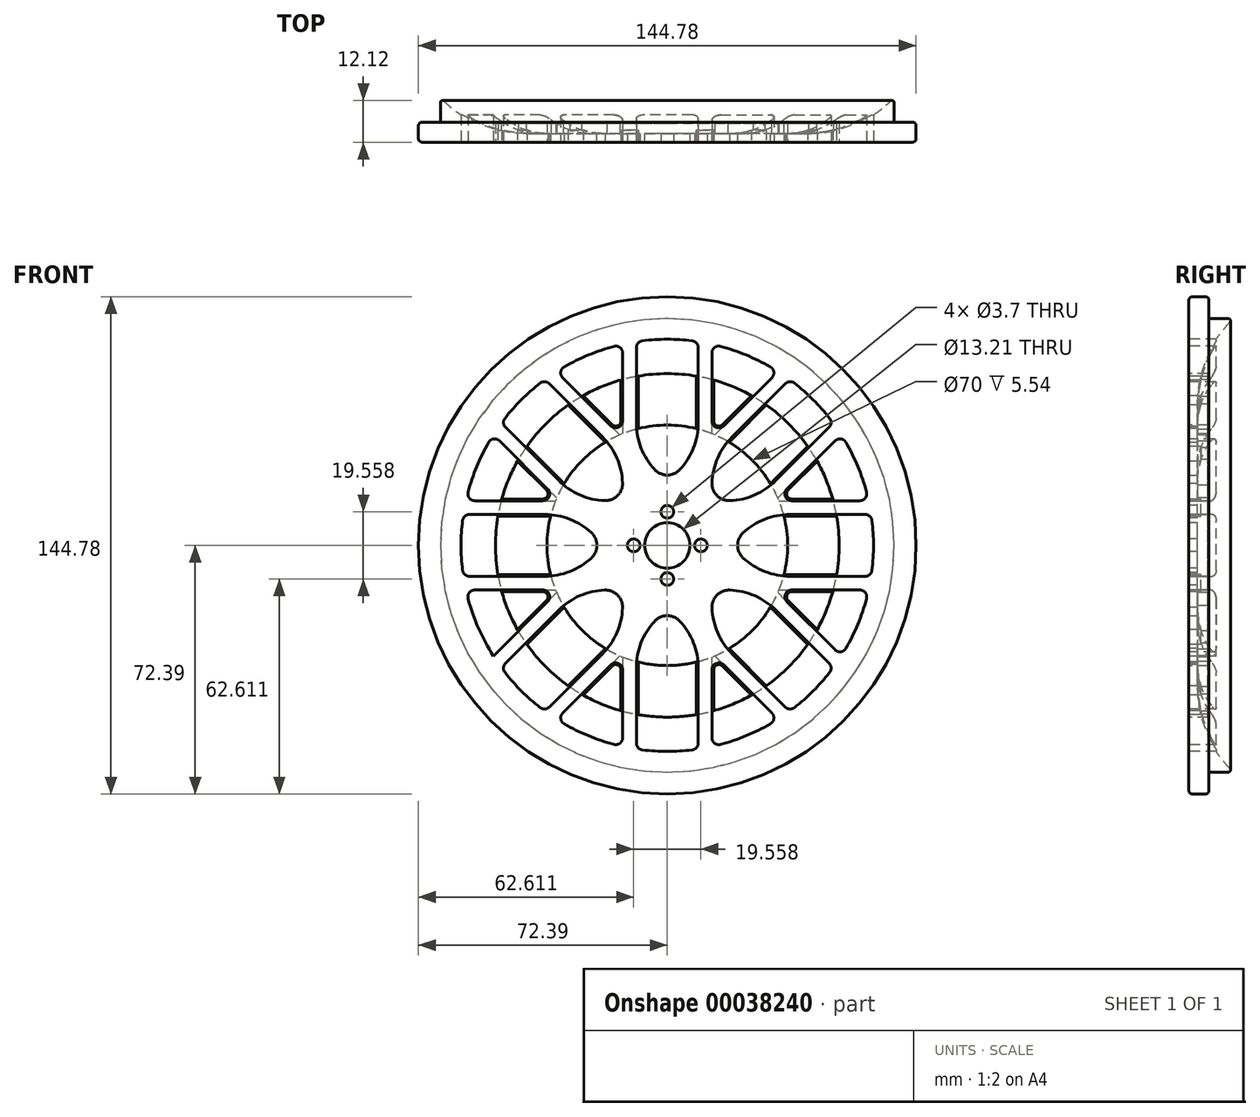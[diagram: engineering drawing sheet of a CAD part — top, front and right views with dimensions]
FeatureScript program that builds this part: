
annotation { "Feature Type Name" : "Feature", "Feature Type Description" : "" }
export const myFeature = defineFeature(function(context is Context, id is Id, definition is map)
    precondition{}
    {
        {
            var Q0;
            Q0=qCreatedBy(makeId("Right.planeOp"),FACE);
            var sketch = newSketch(context, id + "F0", { "sketchPlane" : qUnion([Q0])});
            skLineSegment(sketch, "E0", {"start": v(0, 6.6) * mm, "end": v(2.54, 6.6) * mm});
            skLineSegment(sketch, "E1", {"start": v(2.54, 6.6) * mm, "end": v(2.54, 42) * mm});
            skLineSegment(sketch, "E2", {"start": v(0, 6.6) * mm, "end": v(0, 66) * mm});
            skLineSegment(sketch, "E3", {"start": v(0, 66) * mm, "end": v(13, 66) * mm});
            skArc(sketch, "E4", {"start": v(2.54, 42) * mm, "mid": v(5.27, 55.1) * mm, "end": v(13, 66) * mm});
            skLineSegment(sketch, "E5", {"start": v(0, 0) * mm, "end": v(13, 0) * mm, "construction": true});
            skSolve(sketch);
        }
        {
            var Q0;
            Q0=makeQuery(id+"F0.imprint","IMPRINT",FACE,{"disambiguationData":[TD([[makeQuery(id+"F0.imprint","IMPRINT",EDGE,{"derivedFrom":sQuery(id+"F0.wireOp",EDGE,"E0")}),1.0]])]});
            var Q1;
            Q1=sQuery(id+"F0.wireOp",EDGE,"E5");
            revolve(context, id + "F1", {"entities" : qUnion([Q0]), "axis" : qUnion([Q1]), "revolveType" : RevolveType.FULL});
        }
        {
            var Q0;
            Q0=qCreatedBy(makeId("Front.planeOp"),FACE);
            var sketch = newSketch(context, id + "F2", { "sketchPlane" : qUnion([Q0])});
            skCircle(sketch, "E6", {"center": v(0, 0) * mm, "radius": 9.78 * mm, "construction": true});
            skPoint(sketch, "E7", {"position": v(0, 9.78) * mm});
            skPoint(sketch, "E8", {"position": v(0, -9.78) * mm});
            skPoint(sketch, "E9", {"position": v(9.78, 0) * mm});
            skPoint(sketch, "E10", {"position": v(-9.78, 0) * mm});
            skSolve(sketch);
        }
        {
            var Q0;
            Q0=sQuery(id+"F2.wireOp",VERTEX,"E7");
            var Q1;
            Q1=sQuery(id+"F2.wireOp",VERTEX,"E9");
            var Q2;
            Q2=sQuery(id+"F2.wireOp",VERTEX,"E8");
            var Q3;
            Q3=sQuery(id+"F2.wireOp",VERTEX,"E10");
            var Q4;
            Q4=makeQuery(id+"F1.opRevolve","SWEPT_BODY",BODY,{"disambiguationData":[OSD([sQuery(id+"F0.wireOp",EDGE,"E0"),sQuery(id+"F0.wireOp",EDGE,"E1"),sQuery(id+"F0.wireOp",EDGE,"E2"),sQuery(id+"F0.wireOp",EDGE,"E3"),sQuery(id+"F0.wireOp",EDGE,"E4")])]});
            hole(context, id + "F3", {"style" : HoleStyle.SIMPLE, "holeDiameter" : 3.7 * mm, "endStyle" : HoleEndStyle.THROUGH, "locations" : qUnion([Q0, Q1, Q2, Q3]), "scope" : qUnion([Q4])});
        }
        {
            var Q0;
            Q0=makeQuery(id+"F1.opRevolve","SWEPT_FACE",FACE,{"disambiguationData":[OSD([sQuery(id+"F0.wireOp",EDGE,"E2")])]});
            var sketch = newSketch(context, id + "F4", { "sketchPlane" : qUnion([Q0])});
            skArc(sketch, "E11", {"start": v(-35.58, 48.31) * mm, "mid": v(-42.43, 42.43) * mm, "end": v(-48.31, 35.58) * mm});
            skLineSegment(sketch, "E12", {"start": v(-58.57, 13) * mm, "end": v(-31.38, 13) * mm});
            skLineSegment(sketch, "E13", {"start": v(-58.57, -13) * mm, "end": v(-31.38, -13) * mm});
            skLineSegment(sketch, "E14", {"start": v(-13, 58.57) * mm, "end": v(-13, 31.38) * mm});
            skLineSegment(sketch, "E15", {"start": v(13, -58.57) * mm, "end": v(13, -31.38) * mm});
            skLineSegment(sketch, "E16", {"start": v(-50.61, 32.23) * mm, "end": v(-31.38, 13) * mm});
            skLineSegment(sketch, "E17", {"start": v(-32.23, 50.61) * mm, "end": v(-13, 31.38) * mm});
            skLineSegment(sketch, "E18", {"start": v(-50.61, -32.23) * mm, "end": v(-31.38, -13) * mm});
            skLineSegment(sketch, "E19", {"start": v(-32.23, -50.61) * mm, "end": v(-13, -31.38) * mm});
            skLineSegment(sketch, "E20.trimOffspring", {"start": v(0, 18.38) * mm, "end": v(9, 27.38) * mm});
            skLineSegment(sketch, "E21.trimOffspring", {"start": v(13, 13) * mm, "end": v(25.73, 13) * mm});
            skLineSegment(sketch, "E22.trimOffspring", {"start": v(18.38, 0) * mm, "end": v(27.38, -9) * mm});
            skLineSegment(sketch, "E23.trimOffspring", {"start": v(13, 13) * mm, "end": v(13, 25.73) * mm});
            skLineSegment(sketch, "E24.trimOffspring", {"start": v(18.38, 0) * mm, "end": v(27.38, 9) * mm});
            skLineSegment(sketch, "E25.trimOffspring", {"start": v(13, -13) * mm, "end": v(25.73, -13) * mm});
            skLineSegment(sketch, "E26.trimOffspring", {"start": v(0, -18.38) * mm, "end": v(9, -27.38) * mm});
            skLineSegment(sketch, "E27.trimOffspring", {"start": v(-13, -13) * mm, "end": v(-13, -25.73) * mm});
            skLineSegment(sketch, "E28.0", {"start": v(-35.58, 48.31) * mm, "end": v(-13, 25.73) * mm});
            skCircle(sketch, "E29.0", {"center": v(0, 0) * mm, "radius": 71 * mm});
            skLineSegment(sketch, "E30.0", {"start": v(-48.31, 35.58) * mm, "end": v(-25.73, 13) * mm});
            skLineSegment(sketch, "E31.0", {"start": v(-9, 59.32) * mm, "end": v(-9, 27.38) * mm});
            skLineSegment(sketch, "E32.0", {"start": v(9, 27.38) * mm, "end": v(9, 59.32) * mm});
            skLineSegment(sketch, "E33.0", {"start": v(13, 25.73) * mm, "end": v(35.58, 48.31) * mm});
            skLineSegment(sketch, "E34.0", {"start": v(25.73, 13) * mm, "end": v(48.31, 35.58) * mm});
            skLineSegment(sketch, "E35.0", {"start": v(27.38, 9) * mm, "end": v(59.32, 9) * mm});
            skLineSegment(sketch, "E36.0", {"start": v(27.38, -9) * mm, "end": v(59.32, -9) * mm});
            skLineSegment(sketch, "E37.0", {"start": v(25.73, -13) * mm, "end": v(48.31, -35.58) * mm});
            skLineSegment(sketch, "E38.0", {"start": v(13, -25.73) * mm, "end": v(35.58, -48.31) * mm});
            skLineSegment(sketch, "E39.0", {"start": v(9, -59.32) * mm, "end": v(9, -27.38) * mm});
            skLineSegment(sketch, "E40.0", {"start": v(-9, -27.38) * mm, "end": v(-9, -59.32) * mm});
            skLineSegment(sketch, "E41.0", {"start": v(-35.58, -48.31) * mm, "end": v(-13, -25.73) * mm});
            skLineSegment(sketch, "E42.0", {"start": v(-48.31, -35.58) * mm, "end": v(-25.73, -13) * mm});
            skLineSegment(sketch, "E43.0", {"start": v(-59.32, -9) * mm, "end": v(-27.38, -9) * mm});
            skLineSegment(sketch, "E44.0", {"start": v(-59.32, 9) * mm, "end": v(-27.38, 9) * mm});
            skLineSegment(sketch, "E45.trimOffspring", {"start": v(-25.73, 13) * mm, "end": v(-13, 13) * mm});
            skLineSegment(sketch, "E46.trimOffspring", {"start": v(-27.38, 9) * mm, "end": v(-18.38, 0) * mm});
            skLineSegment(sketch, "E47.trimOffspring", {"start": v(-27.38, -9) * mm, "end": v(-18.38, 0) * mm});
            skLineSegment(sketch, "E48.trimOffspring", {"start": v(-25.73, -13) * mm, "end": v(-13, -13) * mm});
            skLineSegment(sketch, "E49.trimOffspring", {"start": v(-9, -27.38) * mm, "end": v(0, -18.38) * mm});
            skLineSegment(sketch, "E50.trimOffspring", {"start": v(-13, -31.38) * mm, "end": v(-13, -58.57) * mm});
            skLineSegment(sketch, "E51.trimOffspring", {"start": v(13, -31.38) * mm, "end": v(32.23, -50.61) * mm});
            skLineSegment(sketch, "E52.trimOffspring", {"start": v(13, -25.73) * mm, "end": v(13, -13) * mm});
            skLineSegment(sketch, "E53.trimOffspring", {"start": v(31.38, -13) * mm, "end": v(50.61, -32.23) * mm});
            skLineSegment(sketch, "E54.trimOffspring", {"start": v(31.38, -13) * mm, "end": v(58.57, -13) * mm});
            skLineSegment(sketch, "E55.trimOffspring", {"start": v(31.38, 13) * mm, "end": v(50.61, 32.23) * mm});
            skLineSegment(sketch, "E56.trimOffspring", {"start": v(31.38, 13) * mm, "end": v(58.57, 13) * mm});
            skLineSegment(sketch, "E57.trimOffspring", {"start": v(13, 31.38) * mm, "end": v(13, 58.57) * mm});
            skLineSegment(sketch, "E58.trimOffspring", {"start": v(13, 31.38) * mm, "end": v(32.23, 50.61) * mm});
            skLineSegment(sketch, "E59.trimOffspring", {"start": v(-9, 27.38) * mm, "end": v(0, 18.38) * mm});
            skLineSegment(sketch, "E60.trimOffspring", {"start": v(-13, 25.73) * mm, "end": v(-13, 13) * mm});
            skArc(sketch, "E61.trimOffspring", {"start": v(-50.61, 32.23) * mm, "mid": v(-55.43, 22.96) * mm, "end": v(-58.57, 13) * mm});
            skArc(sketch, "E62.trimOffspring", {"start": v(-13, 58.57) * mm, "mid": v(-22.96, 55.43) * mm, "end": v(-32.23, 50.61) * mm});
            skArc(sketch, "E63.trimOffspring", {"start": v(9, 59.32) * mm, "mid": v(0, 60) * mm, "end": v(-9, 59.32) * mm});
            skArc(sketch, "E64.trimOffspring", {"start": v(32.23, 50.61) * mm, "mid": v(22.96, 55.43) * mm, "end": v(13, 58.57) * mm});
            skArc(sketch, "E65.trimOffspring", {"start": v(48.31, 35.58) * mm, "mid": v(42.43, 42.43) * mm, "end": v(35.58, 48.31) * mm});
            skArc(sketch, "E66.trimOffspring", {"start": v(58.57, 13) * mm, "mid": v(55.43, 22.96) * mm, "end": v(50.61, 32.23) * mm});
            skArc(sketch, "E67.trimOffspring", {"start": v(59.32, -9) * mm, "mid": v(60, 0) * mm, "end": v(59.32, 9) * mm});
            skArc(sketch, "E68.trimOffspring", {"start": v(50.61, -32.23) * mm, "mid": v(55.43, -22.96) * mm, "end": v(58.57, -13) * mm});
            skArc(sketch, "E69.trimOffspring", {"start": v(35.58, -48.31) * mm, "mid": v(42.43, -42.43) * mm, "end": v(48.31, -35.58) * mm});
            skArc(sketch, "E70.trimOffspring", {"start": v(13, -58.57) * mm, "mid": v(22.96, -55.43) * mm, "end": v(32.23, -50.61) * mm});
            skArc(sketch, "E71.trimOffspring", {"start": v(-9, -59.32) * mm, "mid": v(0, -60) * mm, "end": v(9, -59.32) * mm});
            skArc(sketch, "E72.trimOffspring", {"start": v(-32.23, -50.61) * mm, "mid": v(-22.96, -55.43) * mm, "end": v(-13, -58.57) * mm});
            skArc(sketch, "E73.trimOffspring", {"start": v(-48.31, -35.58) * mm, "mid": v(-42.43, -42.43) * mm, "end": v(-35.58, -48.31) * mm});
            skArc(sketch, "E74.trimOffspring", {"start": v(-58.57, -13) * mm, "mid": v(-55.43, -22.96) * mm, "end": v(-50.61, -32.23) * mm});
            skArc(sketch, "E75.trimOffspring", {"start": v(-59.32, 9) * mm, "mid": v(-60, 0) * mm, "end": v(-59.32, -9) * mm});
            skSolve(sketch);
        }
        {
            var Q0;
            Q0=makeQuery(id+"F4.imprint","IMPRINT",FACE,{"disambiguationData":[TD([[makeQuery(id+"F4.imprint","IMPRINT",EDGE,{"derivedFrom":sQuery(id+"F4.wireOp",EDGE,"E29.0")}),1.0]])]});
            var Q1;
            Q1=makeQuery(id+"F4.imprint","IMPRINT",FACE,{"disambiguationData":[TD([[makeQuery(id+"F4.imprint","IMPRINT",EDGE,{"derivedFrom":makeQuery(id+"F1.opRevolve","SWEPT_EDGE",EDGE,{"disambiguationData":[OSD([sQuery(id+"F0.wireOp",EDGE,"E0"),sQuery(id+"F0.wireOp",EDGE,"E2")])]})}),1.0]])]});
            var Q2;
            Q2=makeQuery(id+"F4.imprint","IMPRINT",FACE,{"disambiguationData":[TD([[makeQuery(id+"F4.imprint","IMPRINT",EDGE,{"derivedFrom":makeQuery(id+"F3.hole-0.boolean.opBoolean","COPY",EDGE,{"derivedFrom":makeQuery(id+"F3.hole-0.opRevolve","SWEPT_EDGE",EDGE,{"disambiguationData":[OSD([sQuery(id+"F3.hole-0.sketch.wireOp",EDGE,"core_line_2"),sQuery(id+"F3.hole-0.sketch.wireOp",EDGE,"core_line_3")])]})})}),1.0]])]});
            var Q3;
            Q3=makeQuery(id+"F4.imprint","IMPRINT",FACE,{"disambiguationData":[TD([[makeQuery(id+"F4.imprint","IMPRINT",EDGE,{"derivedFrom":makeQuery(id+"F3.hole-1.boolean.opBoolean","COPY",EDGE,{"derivedFrom":makeQuery(id+"F3.hole-1.opRevolve","SWEPT_EDGE",EDGE,{"disambiguationData":[OSD([sQuery(id+"F3.hole-1.sketch.wireOp",EDGE,"core_line_2"),sQuery(id+"F3.hole-1.sketch.wireOp",EDGE,"core_line_3")])]})})}),1.0]])]});
            var Q4;
            Q4=makeQuery(id+"F4.imprint","IMPRINT",FACE,{"disambiguationData":[TD([[makeQuery(id+"F4.imprint","IMPRINT",EDGE,{"derivedFrom":makeQuery(id+"F3.hole-2.boolean.opBoolean","COPY",EDGE,{"derivedFrom":makeQuery(id+"F3.hole-2.opRevolve","SWEPT_EDGE",EDGE,{"disambiguationData":[OSD([sQuery(id+"F3.hole-2.sketch.wireOp",EDGE,"core_line_2"),sQuery(id+"F3.hole-2.sketch.wireOp",EDGE,"core_line_3")])]})})}),1.0]])]});
            var Q5;
            Q5=makeQuery(id+"F4.imprint","IMPRINT",FACE,{"disambiguationData":[TD([[makeQuery(id+"F4.imprint","IMPRINT",EDGE,{"derivedFrom":makeQuery(id+"F3.hole-3.boolean.opBoolean","COPY",EDGE,{"derivedFrom":makeQuery(id+"F3.hole-3.opRevolve","SWEPT_EDGE",EDGE,{"disambiguationData":[OSD([sQuery(id+"F3.hole-3.sketch.wireOp",EDGE,"core_line_2"),sQuery(id+"F3.hole-3.sketch.wireOp",EDGE,"core_line_3")])]})})}),1.0]])]});
            var Q6;
            Q6=makeQuery(id+"F4.imprint","IMPRINT",FACE,{"disambiguationData":[TD([[makeQuery(id+"F4.imprint","IMPRINT",EDGE,{"derivedFrom":sQuery(id+"F4.wireOp",EDGE,"E11")}),1.0]])]});
            var Q7;
            Q7=makeQuery(id+"F4.imprint","IMPRINT",FACE,{"disambiguationData":[TD([[makeQuery(id+"F4.imprint","IMPRINT",EDGE,{"derivedFrom":sQuery(id+"F4.wireOp",EDGE,"E12")}),1.0]])]});
            var Q8;
            Q8=makeQuery(id+"F4.imprint","IMPRINT",FACE,{"disambiguationData":[TD([[makeQuery(id+"F4.imprint","IMPRINT",EDGE,{"derivedFrom":sQuery(id+"F4.wireOp",EDGE,"E43.0")}),1.0]])]});
            var Q9;
            Q9=makeQuery(id+"F4.imprint","IMPRINT",FACE,{"disambiguationData":[TD([[makeQuery(id+"F4.imprint","IMPRINT",EDGE,{"derivedFrom":sQuery(id+"F4.wireOp",EDGE,"E13")}),-1.0]])]});
            var Q10;
            Q10=makeQuery(id+"F4.imprint","IMPRINT",FACE,{"disambiguationData":[TD([[makeQuery(id+"F4.imprint","IMPRINT",EDGE,{"derivedFrom":sQuery(id+"F4.wireOp",EDGE,"E27.trimOffspring")}),-1.0]])]});
            var Q11;
            Q11=makeQuery(id+"F4.imprint","IMPRINT",FACE,{"disambiguationData":[TD([[makeQuery(id+"F4.imprint","IMPRINT",EDGE,{"derivedFrom":sQuery(id+"F4.wireOp",EDGE,"E26.trimOffspring")}),-1.0]])]});
            var Q12;
            Q12=makeQuery(id+"F4.imprint","IMPRINT",FACE,{"disambiguationData":[TD([[makeQuery(id+"F4.imprint","IMPRINT",EDGE,{"derivedFrom":sQuery(id+"F4.wireOp",EDGE,"E15")}),-1.0]])]});
            var Q13;
            Q13=makeQuery(id+"F4.imprint","IMPRINT",FACE,{"disambiguationData":[TD([[makeQuery(id+"F4.imprint","IMPRINT",EDGE,{"derivedFrom":sQuery(id+"F4.wireOp",EDGE,"E25.trimOffspring")}),-1.0]])]});
            var Q14;
            Q14=makeQuery(id+"F4.imprint","IMPRINT",FACE,{"disambiguationData":[TD([[makeQuery(id+"F4.imprint","IMPRINT",EDGE,{"derivedFrom":sQuery(id+"F4.wireOp",EDGE,"E53.trimOffspring")}),1.0]])]});
            var Q15;
            Q15=makeQuery(id+"F4.imprint","IMPRINT",FACE,{"disambiguationData":[TD([[makeQuery(id+"F4.imprint","IMPRINT",EDGE,{"derivedFrom":sQuery(id+"F4.wireOp",EDGE,"E22.trimOffspring")}),1.0]])]});
            var Q16;
            Q16=makeQuery(id+"F4.imprint","IMPRINT",FACE,{"disambiguationData":[TD([[makeQuery(id+"F4.imprint","IMPRINT",EDGE,{"derivedFrom":sQuery(id+"F4.wireOp",EDGE,"E55.trimOffspring")}),-1.0]])]});
            var Q17;
            Q17=makeQuery(id+"F4.imprint","IMPRINT",FACE,{"disambiguationData":[TD([[makeQuery(id+"F4.imprint","IMPRINT",EDGE,{"derivedFrom":sQuery(id+"F4.wireOp",EDGE,"E21.trimOffspring")}),1.0]])]});
            var Q18;
            Q18=makeQuery(id+"F4.imprint","IMPRINT",FACE,{"disambiguationData":[TD([[makeQuery(id+"F4.imprint","IMPRINT",EDGE,{"derivedFrom":sQuery(id+"F4.wireOp",EDGE,"E57.trimOffspring")}),-1.0]])]});
            var Q19;
            Q19=makeQuery(id+"F4.imprint","IMPRINT",FACE,{"disambiguationData":[TD([[makeQuery(id+"F4.imprint","IMPRINT",EDGE,{"derivedFrom":sQuery(id+"F4.wireOp",EDGE,"E20.trimOffspring")}),1.0]])]});
            var Q20;
            Q20=makeQuery(id+"F4.imprint","IMPRINT",FACE,{"disambiguationData":[TD([[makeQuery(id+"F4.imprint","IMPRINT",EDGE,{"derivedFrom":sQuery(id+"F4.wireOp",EDGE,"E14")}),-1.0]])]});
            var Q21;
            Q21=makeQuery(id+"F4.imprint","IMPRINT",FACE,{"disambiguationData":[TD([[makeQuery(id+"F4.imprint","IMPRINT",EDGE,{"derivedFrom":sQuery(id+"F4.wireOp",EDGE,"E19")}),-1.0]])]});
            extrude(context, id + "F5", {"entities" : qUnion([Q0, Q1, Q2, Q3, Q4, Q5, Q6, Q7, Q8, Q9, Q10, Q11, Q12, Q13, Q14, Q15, Q16, Q17, Q18, Q19, Q20, Q21]), "operationType" : NewBodyOperationType.REMOVE, "endBound" : BoundingType.THROUGH_ALL, "oppositeDirection" : true, "depth" : 25 * mm});
        }
        {
            var Q0;
            Q0=makeQuery(id+"F5.boolean.opBoolean","COPY",EDGE,{"derivedFrom":makeQuery(id+"F5.opExtrude","SWEPT_EDGE",EDGE,{"disambiguationData":[OSD([sQuery(id+"F4.wireOp",EDGE,"E31.0"),sQuery(id+"F4.wireOp",EDGE,"E59.trimOffspring")])]})});
            var Q1;
            Q1=makeQuery(id+"F5.boolean.opBoolean","COPY",EDGE,{"derivedFrom":makeQuery(id+"F5.opExtrude","SWEPT_EDGE",EDGE,{"disambiguationData":[OSD([sQuery(id+"F4.wireOp",EDGE,"E20.trimOffspring"),sQuery(id+"F4.wireOp",EDGE,"E32.0")])]})});
            var Q2;
            Q2=makeQuery(id+"F5.boolean.opBoolean","COPY",EDGE,{"derivedFrom":makeQuery(id+"F5.opExtrude","SWEPT_EDGE",EDGE,{"disambiguationData":[OSD([sQuery(id+"F4.wireOp",EDGE,"E23.trimOffspring"),sQuery(id+"F4.wireOp",EDGE,"E33.0")])]})});
            var Q3;
            Q3=makeQuery(id+"F5.boolean.opBoolean","COPY",EDGE,{"derivedFrom":makeQuery(id+"F5.opExtrude","SWEPT_EDGE",EDGE,{"disambiguationData":[OSD([sQuery(id+"F4.wireOp",EDGE,"E21.trimOffspring"),sQuery(id+"F4.wireOp",EDGE,"E34.0")])]})});
            var Q4;
            Q4=makeQuery(id+"F5.boolean.opBoolean","COPY",EDGE,{"derivedFrom":makeQuery(id+"F5.opExtrude","SWEPT_EDGE",EDGE,{"disambiguationData":[OSD([sQuery(id+"F4.wireOp",EDGE,"E24.trimOffspring"),sQuery(id+"F4.wireOp",EDGE,"E35.0")])]})});
            var Q5;
            Q5=makeQuery(id+"F5.boolean.opBoolean","COPY",EDGE,{"derivedFrom":makeQuery(id+"F5.opExtrude","SWEPT_EDGE",EDGE,{"disambiguationData":[OSD([sQuery(id+"F4.wireOp",EDGE,"E22.trimOffspring"),sQuery(id+"F4.wireOp",EDGE,"E36.0")])]})});
            var Q6;
            Q6=makeQuery(id+"F5.boolean.opBoolean","COPY",EDGE,{"derivedFrom":makeQuery(id+"F5.opExtrude","SWEPT_EDGE",EDGE,{"disambiguationData":[OSD([sQuery(id+"F4.wireOp",EDGE,"E25.trimOffspring"),sQuery(id+"F4.wireOp",EDGE,"E37.0")])]})});
            var Q7;
            Q7=makeQuery(id+"F5.boolean.opBoolean","COPY",EDGE,{"derivedFrom":makeQuery(id+"F5.opExtrude","SWEPT_EDGE",EDGE,{"disambiguationData":[OSD([sQuery(id+"F4.wireOp",EDGE,"E26.trimOffspring"),sQuery(id+"F4.wireOp",EDGE,"E39.0")])]})});
            var Q8;
            Q8=makeQuery(id+"F5.boolean.opBoolean","COPY",EDGE,{"derivedFrom":makeQuery(id+"F5.opExtrude","SWEPT_EDGE",EDGE,{"disambiguationData":[OSD([sQuery(id+"F4.wireOp",EDGE,"E38.0"),sQuery(id+"F4.wireOp",EDGE,"E52.trimOffspring")])]})});
            var Q9;
            Q9=makeQuery(id+"F5.boolean.opBoolean","COPY",EDGE,{"derivedFrom":makeQuery(id+"F5.opExtrude","SWEPT_EDGE",EDGE,{"disambiguationData":[OSD([sQuery(id+"F4.wireOp",EDGE,"E40.0"),sQuery(id+"F4.wireOp",EDGE,"E49.trimOffspring")])]})});
            var Q10;
            Q10=makeQuery(id+"F5.boolean.opBoolean","COPY",EDGE,{"derivedFrom":makeQuery(id+"F5.opExtrude","SWEPT_EDGE",EDGE,{"disambiguationData":[OSD([sQuery(id+"F4.wireOp",EDGE,"E27.trimOffspring"),sQuery(id+"F4.wireOp",EDGE,"E41.0")])]})});
            var Q11;
            Q11=makeQuery(id+"F5.boolean.opBoolean","COPY",EDGE,{"derivedFrom":makeQuery(id+"F5.opExtrude","SWEPT_EDGE",EDGE,{"disambiguationData":[OSD([sQuery(id+"F4.wireOp",EDGE,"E43.0"),sQuery(id+"F4.wireOp",EDGE,"E47.trimOffspring")])]})});
            var Q12;
            Q12=makeQuery(id+"F5.boolean.opBoolean","COPY",EDGE,{"derivedFrom":makeQuery(id+"F5.opExtrude","SWEPT_EDGE",EDGE,{"disambiguationData":[OSD([sQuery(id+"F4.wireOp",EDGE,"E42.0"),sQuery(id+"F4.wireOp",EDGE,"E48.trimOffspring")])]})});
            var Q13;
            Q13=makeQuery(id+"F5.boolean.opBoolean","COPY",EDGE,{"derivedFrom":makeQuery(id+"F5.opExtrude","SWEPT_EDGE",EDGE,{"disambiguationData":[OSD([sQuery(id+"F4.wireOp",EDGE,"E44.0"),sQuery(id+"F4.wireOp",EDGE,"E46.trimOffspring")])]})});
            var Q14;
            Q14=makeQuery(id+"F5.boolean.opBoolean","COPY",EDGE,{"derivedFrom":makeQuery(id+"F5.opExtrude","SWEPT_EDGE",EDGE,{"disambiguationData":[OSD([sQuery(id+"F4.wireOp",EDGE,"E28.0"),sQuery(id+"F4.wireOp",EDGE,"E60.trimOffspring")])]})});
            var Q15;
            Q15=makeQuery(id+"F5.boolean.opBoolean","COPY",EDGE,{"derivedFrom":makeQuery(id+"F5.opExtrude","SWEPT_EDGE",EDGE,{"disambiguationData":[OSD([sQuery(id+"F4.wireOp",EDGE,"E30.0"),sQuery(id+"F4.wireOp",EDGE,"E45.trimOffspring")])]})});
            fillet(context, id + "F6", {"entities" : qUnion([Q0, Q1, Q2, Q3, Q4, Q5, Q6, Q7, Q8, Q9, Q10, Q11, Q12, Q13, Q14, Q15]), "radius" : 20 * mm, "tangentPropagation" : true, "allowEdgeOverflow" : false});
        }
        {
            var Q0;
            Q0=makeQuery(id+"F5.boolean.opBoolean","COPY",EDGE,{"derivedFrom":makeQuery(id+"F5.opExtrude","SWEPT_EDGE",EDGE,{"disambiguationData":[OSD([sQuery(id+"F4.wireOp",EDGE,"E22.trimOffspring"),sQuery(id+"F4.wireOp",EDGE,"E24.trimOffspring")])]})});
            var Q1;
            Q1=makeQuery(id+"F5.boolean.opBoolean","COPY",EDGE,{"derivedFrom":makeQuery(id+"F5.opExtrude","SWEPT_EDGE",EDGE,{"disambiguationData":[OSD([sQuery(id+"F4.wireOp",EDGE,"E21.trimOffspring"),sQuery(id+"F4.wireOp",EDGE,"E23.trimOffspring")])]})});
            var Q2;
            Q2=makeQuery(id+"F5.boolean.opBoolean","COPY",EDGE,{"derivedFrom":makeQuery(id+"F5.opExtrude","SWEPT_EDGE",EDGE,{"disambiguationData":[OSD([sQuery(id+"F4.wireOp",EDGE,"E20.trimOffspring"),sQuery(id+"F4.wireOp",EDGE,"E59.trimOffspring")])]})});
            var Q3;
            Q3=makeQuery(id+"F5.boolean.opBoolean","COPY",EDGE,{"derivedFrom":makeQuery(id+"F5.opExtrude","SWEPT_EDGE",EDGE,{"disambiguationData":[OSD([sQuery(id+"F4.wireOp",EDGE,"E45.trimOffspring"),sQuery(id+"F4.wireOp",EDGE,"E60.trimOffspring")])]})});
            var Q4;
            Q4=makeQuery(id+"F5.boolean.opBoolean","COPY",EDGE,{"derivedFrom":makeQuery(id+"F5.opExtrude","SWEPT_EDGE",EDGE,{"disambiguationData":[OSD([sQuery(id+"F4.wireOp",EDGE,"E46.trimOffspring"),sQuery(id+"F4.wireOp",EDGE,"E47.trimOffspring")])]})});
            var Q5;
            Q5=makeQuery(id+"F5.boolean.opBoolean","COPY",EDGE,{"derivedFrom":makeQuery(id+"F5.opExtrude","SWEPT_EDGE",EDGE,{"disambiguationData":[OSD([sQuery(id+"F4.wireOp",EDGE,"E27.trimOffspring"),sQuery(id+"F4.wireOp",EDGE,"E48.trimOffspring")])]})});
            var Q6;
            Q6=makeQuery(id+"F5.boolean.opBoolean","COPY",EDGE,{"derivedFrom":makeQuery(id+"F5.opExtrude","SWEPT_EDGE",EDGE,{"disambiguationData":[OSD([sQuery(id+"F4.wireOp",EDGE,"E26.trimOffspring"),sQuery(id+"F4.wireOp",EDGE,"E49.trimOffspring")])]})});
            var Q7;
            Q7=makeQuery(id+"F5.boolean.opBoolean","COPY",EDGE,{"derivedFrom":makeQuery(id+"F5.opExtrude","SWEPT_EDGE",EDGE,{"disambiguationData":[OSD([sQuery(id+"F4.wireOp",EDGE,"E25.trimOffspring"),sQuery(id+"F4.wireOp",EDGE,"E52.trimOffspring")])]})});
            fillet(context, id + "F7", {"entities" : qUnion([Q0, Q1, Q2, Q3, Q4, Q5, Q6, Q7]), "radius" : 5 * mm, "tangentPropagation" : true, "allowEdgeOverflow" : false});
        }
        {
            var Q0;
            Q0=makeQuery(id+"F5.boolean.opBoolean","COPY",EDGE,{"derivedFrom":makeQuery(id+"F5.opExtrude","SWEPT_EDGE",EDGE,{"disambiguationData":[OSD([sQuery(id+"F4.wireOp",EDGE,"E12"),sQuery(id+"F4.wireOp",EDGE,"E16")])]})});
            var Q1;
            Q1=makeQuery(id+"F5.boolean.opBoolean","COPY",EDGE,{"derivedFrom":makeQuery(id+"F5.opExtrude","SWEPT_EDGE",EDGE,{"disambiguationData":[OSD([sQuery(id+"F4.wireOp",EDGE,"E14"),sQuery(id+"F4.wireOp",EDGE,"E17")])]})});
            var Q2;
            Q2=makeQuery(id+"F5.boolean.opBoolean","COPY",EDGE,{"derivedFrom":makeQuery(id+"F5.opExtrude","SWEPT_EDGE",EDGE,{"disambiguationData":[OSD([sQuery(id+"F4.wireOp",EDGE,"E57.trimOffspring"),sQuery(id+"F4.wireOp",EDGE,"E58.trimOffspring")])]})});
            var Q3;
            Q3=makeQuery(id+"F5.boolean.opBoolean","COPY",EDGE,{"derivedFrom":makeQuery(id+"F5.opExtrude","SWEPT_EDGE",EDGE,{"disambiguationData":[OSD([sQuery(id+"F4.wireOp",EDGE,"E55.trimOffspring"),sQuery(id+"F4.wireOp",EDGE,"E56.trimOffspring")])]})});
            var Q4;
            Q4=makeQuery(id+"F5.boolean.opBoolean","COPY",EDGE,{"derivedFrom":makeQuery(id+"F5.opExtrude","SWEPT_EDGE",EDGE,{"disambiguationData":[OSD([sQuery(id+"F4.wireOp",EDGE,"E53.trimOffspring"),sQuery(id+"F4.wireOp",EDGE,"E54.trimOffspring")])]})});
            var Q5;
            Q5=makeQuery(id+"F5.boolean.opBoolean","COPY",EDGE,{"derivedFrom":makeQuery(id+"F5.opExtrude","SWEPT_EDGE",EDGE,{"disambiguationData":[OSD([sQuery(id+"F4.wireOp",EDGE,"E15"),sQuery(id+"F4.wireOp",EDGE,"E51.trimOffspring")])]})});
            var Q6;
            Q6=makeQuery(id+"F5.boolean.opBoolean","COPY",EDGE,{"derivedFrom":makeQuery(id+"F5.opExtrude","SWEPT_EDGE",EDGE,{"disambiguationData":[OSD([sQuery(id+"F4.wireOp",EDGE,"E19"),sQuery(id+"F4.wireOp",EDGE,"E50.trimOffspring")])]})});
            var Q7;
            Q7=makeQuery(id+"F5.boolean.opBoolean","COPY",EDGE,{"derivedFrom":makeQuery(id+"F5.opExtrude","SWEPT_EDGE",EDGE,{"disambiguationData":[OSD([sQuery(id+"F4.wireOp",EDGE,"E13"),sQuery(id+"F4.wireOp",EDGE,"E18")])]})});
            var Q8;
            Q8=makeQuery(id+"F5.boolean.opBoolean","COPY",EDGE,{"derivedFrom":makeQuery(id+"F5.opExtrude","SWEPT_EDGE",EDGE,{"disambiguationData":[OSD([sQuery(id+"F4.wireOp",EDGE,"E14"),sQuery(id+"F4.wireOp",EDGE,"E62.trimOffspring")])]})});
            var Q9;
            Q9=makeQuery(id+"F5.boolean.opBoolean","COPY",EDGE,{"derivedFrom":makeQuery(id+"F5.opExtrude","SWEPT_EDGE",EDGE,{"disambiguationData":[OSD([sQuery(id+"F4.wireOp",EDGE,"E31.0"),sQuery(id+"F4.wireOp",EDGE,"E63.trimOffspring")])]})});
            var Q10;
            Q10=makeQuery(id+"F5.boolean.opBoolean","COPY",EDGE,{"derivedFrom":makeQuery(id+"F5.opExtrude","SWEPT_EDGE",EDGE,{"disambiguationData":[OSD([sQuery(id+"F4.wireOp",EDGE,"E17"),sQuery(id+"F4.wireOp",EDGE,"E62.trimOffspring")])]})});
            var Q11;
            Q11=makeQuery(id+"F5.boolean.opBoolean","COPY",EDGE,{"derivedFrom":makeQuery(id+"F5.opExtrude","SWEPT_EDGE",EDGE,{"disambiguationData":[OSD([sQuery(id+"F4.wireOp",EDGE,"E11"),sQuery(id+"F4.wireOp",EDGE,"E28.0")])]})});
            var Q12;
            Q12=makeQuery(id+"F5.boolean.opBoolean","COPY",EDGE,{"derivedFrom":makeQuery(id+"F5.opExtrude","SWEPT_EDGE",EDGE,{"disambiguationData":[OSD([sQuery(id+"F4.wireOp",EDGE,"E11"),sQuery(id+"F4.wireOp",EDGE,"E30.0")])]})});
            var Q13;
            Q13=makeQuery(id+"F5.boolean.opBoolean","COPY",EDGE,{"derivedFrom":makeQuery(id+"F5.opExtrude","SWEPT_EDGE",EDGE,{"disambiguationData":[OSD([sQuery(id+"F4.wireOp",EDGE,"E16"),sQuery(id+"F4.wireOp",EDGE,"E61.trimOffspring")])]})});
            var Q14;
            Q14=makeQuery(id+"F5.boolean.opBoolean","COPY",EDGE,{"derivedFrom":makeQuery(id+"F5.opExtrude","SWEPT_EDGE",EDGE,{"disambiguationData":[OSD([sQuery(id+"F4.wireOp",EDGE,"E12"),sQuery(id+"F4.wireOp",EDGE,"E61.trimOffspring")])]})});
            var Q15;
            Q15=makeQuery(id+"F5.boolean.opBoolean","COPY",EDGE,{"derivedFrom":makeQuery(id+"F5.opExtrude","SWEPT_EDGE",EDGE,{"disambiguationData":[OSD([sQuery(id+"F4.wireOp",EDGE,"E43.0"),sQuery(id+"F4.wireOp",EDGE,"E75.trimOffspring")])]})});
            var Q16;
            Q16=makeQuery(id+"F5.boolean.opBoolean","COPY",EDGE,{"derivedFrom":makeQuery(id+"F5.opExtrude","SWEPT_EDGE",EDGE,{"disambiguationData":[OSD([sQuery(id+"F4.wireOp",EDGE,"E13"),sQuery(id+"F4.wireOp",EDGE,"E74.trimOffspring")])]})});
            var Q17;
            Q17=makeQuery(id+"F5.boolean.opBoolean","COPY",EDGE,{"derivedFrom":makeQuery(id+"F5.opExtrude","SWEPT_EDGE",EDGE,{"disambiguationData":[OSD([sQuery(id+"F4.wireOp",EDGE,"E42.0"),sQuery(id+"F4.wireOp",EDGE,"E73.trimOffspring")])]})});
            var Q18;
            Q18=makeQuery(id+"F5.boolean.opBoolean","COPY",EDGE,{"derivedFrom":makeQuery(id+"F5.opExtrude","SWEPT_EDGE",EDGE,{"disambiguationData":[OSD([sQuery(id+"F4.wireOp",EDGE,"E44.0"),sQuery(id+"F4.wireOp",EDGE,"E75.trimOffspring")])]})});
            var Q19;
            Q19=makeQuery(id+"F5.boolean.opBoolean","COPY",EDGE,{"derivedFrom":makeQuery(id+"F5.opExtrude","SWEPT_EDGE",EDGE,{"disambiguationData":[OSD([sQuery(id+"F4.wireOp",EDGE,"E41.0"),sQuery(id+"F4.wireOp",EDGE,"E73.trimOffspring")])]})});
            var Q20;
            Q20=makeQuery(id+"F5.boolean.opBoolean","COPY",EDGE,{"derivedFrom":makeQuery(id+"F5.opExtrude","SWEPT_EDGE",EDGE,{"disambiguationData":[OSD([sQuery(id+"F4.wireOp",EDGE,"E19"),sQuery(id+"F4.wireOp",EDGE,"E72.trimOffspring")])]})});
            var Q21;
            Q21=makeQuery(id+"F5.boolean.opBoolean","COPY",EDGE,{"derivedFrom":makeQuery(id+"F5.opExtrude","SWEPT_EDGE",EDGE,{"disambiguationData":[OSD([sQuery(id+"F4.wireOp",EDGE,"E40.0"),sQuery(id+"F4.wireOp",EDGE,"E71.trimOffspring")])]})});
            var Q22;
            Q22=makeQuery(id+"F5.boolean.opBoolean","COPY",EDGE,{"derivedFrom":makeQuery(id+"F5.opExtrude","SWEPT_EDGE",EDGE,{"disambiguationData":[OSD([sQuery(id+"F4.wireOp",EDGE,"E15"),sQuery(id+"F4.wireOp",EDGE,"E70.trimOffspring")])]})});
            var Q23;
            Q23=makeQuery(id+"F5.boolean.opBoolean","COPY",EDGE,{"derivedFrom":makeQuery(id+"F5.opExtrude","SWEPT_EDGE",EDGE,{"disambiguationData":[OSD([sQuery(id+"F4.wireOp",EDGE,"E50.trimOffspring"),sQuery(id+"F4.wireOp",EDGE,"E72.trimOffspring")])]})});
            var Q24;
            Q24=makeQuery(id+"F5.boolean.opBoolean","COPY",EDGE,{"derivedFrom":makeQuery(id+"F5.opExtrude","SWEPT_EDGE",EDGE,{"disambiguationData":[OSD([sQuery(id+"F4.wireOp",EDGE,"E39.0"),sQuery(id+"F4.wireOp",EDGE,"E71.trimOffspring")])]})});
            var Q25;
            Q25=makeQuery(id+"F5.boolean.opBoolean","COPY",EDGE,{"derivedFrom":makeQuery(id+"F5.opExtrude","SWEPT_EDGE",EDGE,{"disambiguationData":[OSD([sQuery(id+"F4.wireOp",EDGE,"E51.trimOffspring"),sQuery(id+"F4.wireOp",EDGE,"E70.trimOffspring")])]})});
            var Q26;
            Q26=makeQuery(id+"F5.boolean.opBoolean","COPY",EDGE,{"derivedFrom":makeQuery(id+"F5.opExtrude","SWEPT_EDGE",EDGE,{"disambiguationData":[OSD([sQuery(id+"F4.wireOp",EDGE,"E37.0"),sQuery(id+"F4.wireOp",EDGE,"E69.trimOffspring")])]})});
            var Q27;
            Q27=makeQuery(id+"F5.boolean.opBoolean","COPY",EDGE,{"derivedFrom":makeQuery(id+"F5.opExtrude","SWEPT_EDGE",EDGE,{"disambiguationData":[OSD([sQuery(id+"F4.wireOp",EDGE,"E36.0"),sQuery(id+"F4.wireOp",EDGE,"E67.trimOffspring")])]})});
            var Q28;
            Q28=makeQuery(id+"F5.boolean.opBoolean","COPY",EDGE,{"derivedFrom":makeQuery(id+"F5.opExtrude","SWEPT_EDGE",EDGE,{"disambiguationData":[OSD([sQuery(id+"F4.wireOp",EDGE,"E38.0"),sQuery(id+"F4.wireOp",EDGE,"E69.trimOffspring")])]})});
            var Q29;
            Q29=makeQuery(id+"F5.boolean.opBoolean","COPY",EDGE,{"derivedFrom":makeQuery(id+"F5.opExtrude","SWEPT_EDGE",EDGE,{"disambiguationData":[OSD([sQuery(id+"F4.wireOp",EDGE,"E53.trimOffspring"),sQuery(id+"F4.wireOp",EDGE,"E68.trimOffspring")])]})});
            var Q30;
            Q30=makeQuery(id+"F5.boolean.opBoolean","COPY",EDGE,{"derivedFrom":makeQuery(id+"F5.opExtrude","SWEPT_EDGE",EDGE,{"disambiguationData":[OSD([sQuery(id+"F4.wireOp",EDGE,"E54.trimOffspring"),sQuery(id+"F4.wireOp",EDGE,"E68.trimOffspring")])]})});
            var Q31;
            Q31=makeQuery(id+"F5.boolean.opBoolean","COPY",EDGE,{"derivedFrom":makeQuery(id+"F5.opExtrude","SWEPT_EDGE",EDGE,{"disambiguationData":[OSD([sQuery(id+"F4.wireOp",EDGE,"E35.0"),sQuery(id+"F4.wireOp",EDGE,"E67.trimOffspring")])]})});
            var Q32;
            Q32=makeQuery(id+"F5.boolean.opBoolean","COPY",EDGE,{"derivedFrom":makeQuery(id+"F5.opExtrude","SWEPT_EDGE",EDGE,{"disambiguationData":[OSD([sQuery(id+"F4.wireOp",EDGE,"E56.trimOffspring"),sQuery(id+"F4.wireOp",EDGE,"E66.trimOffspring")])]})});
            var Q33;
            Q33=makeQuery(id+"F5.boolean.opBoolean","COPY",EDGE,{"derivedFrom":makeQuery(id+"F5.opExtrude","SWEPT_EDGE",EDGE,{"disambiguationData":[OSD([sQuery(id+"F4.wireOp",EDGE,"E55.trimOffspring"),sQuery(id+"F4.wireOp",EDGE,"E66.trimOffspring")])]})});
            var Q34;
            Q34=makeQuery(id+"F5.boolean.opBoolean","COPY",EDGE,{"derivedFrom":makeQuery(id+"F5.opExtrude","SWEPT_EDGE",EDGE,{"disambiguationData":[OSD([sQuery(id+"F4.wireOp",EDGE,"E34.0"),sQuery(id+"F4.wireOp",EDGE,"E65.trimOffspring")])]})});
            var Q35;
            Q35=makeQuery(id+"F5.boolean.opBoolean","COPY",EDGE,{"derivedFrom":makeQuery(id+"F5.opExtrude","SWEPT_EDGE",EDGE,{"disambiguationData":[OSD([sQuery(id+"F4.wireOp",EDGE,"E33.0"),sQuery(id+"F4.wireOp",EDGE,"E65.trimOffspring")])]})});
            var Q36;
            Q36=makeQuery(id+"F5.boolean.opBoolean","COPY",EDGE,{"derivedFrom":makeQuery(id+"F5.opExtrude","SWEPT_EDGE",EDGE,{"disambiguationData":[OSD([sQuery(id+"F4.wireOp",EDGE,"E58.trimOffspring"),sQuery(id+"F4.wireOp",EDGE,"E64.trimOffspring")])]})});
            var Q37;
            Q37=makeQuery(id+"F5.boolean.opBoolean","COPY",EDGE,{"derivedFrom":makeQuery(id+"F5.opExtrude","SWEPT_EDGE",EDGE,{"disambiguationData":[OSD([sQuery(id+"F4.wireOp",EDGE,"E57.trimOffspring"),sQuery(id+"F4.wireOp",EDGE,"E64.trimOffspring")])]})});
            var Q38;
            Q38=makeQuery(id+"F5.boolean.opBoolean","COPY",EDGE,{"derivedFrom":makeQuery(id+"F5.opExtrude","SWEPT_EDGE",EDGE,{"disambiguationData":[OSD([sQuery(id+"F4.wireOp",EDGE,"E32.0"),sQuery(id+"F4.wireOp",EDGE,"E63.trimOffspring")])]})});
            fillet(context, id + "F8", {"entities" : qUnion([Q0, Q1, Q2, Q3, Q4, Q5, Q6, Q7, Q8, Q9, Q10, Q11, Q12, Q13, Q14, Q15, Q16, Q17, Q18, Q19, Q20, Q21, Q22, Q23, Q24, Q25, Q26, Q27, Q28, Q29, Q30, Q31, Q32, Q33, Q34, Q35, Q36, Q37, Q38]), "radius" : 2 * mm, "tangentPropagation" : true, "allowEdgeOverflow" : false});
        }
        {
            var Q0;
            Q0=makeQuery(id+"F1.opRevolve","SWEPT_EDGE",EDGE,{"disambiguationData":[OSD([sQuery(id+"F0.wireOp",EDGE,"E3"),sQuery(id+"F0.wireOp",EDGE,"E4")])]});
            fillet(context, id + "F9", {"entities" : qUnion([Q0]), "radius" : .6 * mm, "tangentPropagation" : true, "allowEdgeOverflow" : false});
        }
        {
            var Q0;
            Q0=qCreatedBy(makeId("Right.planeOp"),FACE);
            var sketch = newSketch(context, id + "F10", { "sketchPlane" : qUnion([Q0])});
            skArc(sketch, "E76", {"start": v(3.53, 50) * mm, "mid": v(2.79, 46.03) * mm, "end": v(2.54, 42) * mm});
            skLineSegment(sketch, "E77", {"start": v(2.54, 35) * mm, "end": v(2.54, 42) * mm});
            skLineSegment(sketch, "E78", {"start": v(2.54, 35) * mm, "end": v(5.54, 35) * mm});
            skLineSegment(sketch, "E79", {"start": v(5.54, 35) * mm, "end": v(5.54, 50) * mm});
            skLineSegment(sketch, "E80", {"start": v(5.54, 50) * mm, "end": v(3.53, 50) * mm});
            skLineSegment(sketch, "E81", {"start": v(0, 0) * mm, "end": v(5.54, 0) * mm, "construction": true});
            skSolve(sketch);
        }
        {
            var Q0;
            Q0 = qSketchRegion(id + "F10", true);
            var Q1;
            Q1=sQuery(id+"F10.wireOp",EDGE,"E81");
            revolve(context, id + "F11", {"entities" : qUnion([Q0]), "axis" : qUnion([Q1]), "revolveType" : RevolveType.FULL});
        }
        {
            var Q0;
            Q0=makeQuery(id+"F1.opRevolve","SWEPT_FACE",FACE,{"disambiguationData":[OSD([sQuery(id+"F0.wireOp",EDGE,"E2")])]});
            var sketch = newSketch(context, id + "F12", { "sketchPlane" : qUnion([Q0])});
            skArc(sketch, "E82.0", {"start": v(-18.06, 29.98) * mm, "mid": v(-24.75, 24.75) * mm, "end": v(-29.98, 18.06) * mm});
            skLineSegment(sketch, "E83.0", {"start": v(-34.35, 47.08) * mm, "end": v(-18.86, 31.59) * mm, "construction": true});
            skArc(sketch, "E84.0", {"start": v(-18.86, 31.59) * mm, "mid": v(-14.67, 25.45) * mm, "end": v(-13.01, 18.2) * mm, "construction": true});
            skLineSegment(sketch, "E85.0", {"start": v(-30.42, 48.8) * mm, "end": v(-16.41, 34.8) * mm, "construction": true});
            skLineSegment(sketch, "E86.0", {"start": v(-13, 56.03) * mm, "end": v(-13, 36.21) * mm, "construction": true});
            skArc(sketch, "E87.0", {"start": v(-13, 36.21) * mm, "mid": v(-14.23, 34.37) * mm, "end": v(-16.41, 34.8) * mm, "construction": true});
            skArc(sketch, "E88.0", {"start": v(-18.2, 13.01) * mm, "mid": v(-25.45, 14.67) * mm, "end": v(-31.59, 18.86) * mm, "construction": true});
            skLineSegment(sketch, "E89.0", {"start": v(-47.08, 34.35) * mm, "end": v(-31.59, 18.86) * mm, "construction": true});
            skArc(sketch, "E90.0", {"start": v(-19.21, 31.23) * mm, "mid": v(-18.62, 30.62) * mm, "end": v(-18.06, 29.98) * mm});
            skLineSegment(sketch, "E90.1", {"start": v(-28.83, 40.85) * mm, "end": v(-19.21, 31.23) * mm});
            skLineSegment(sketch, "E91.0", {"start": v(-40.85, 28.83) * mm, "end": v(-31.23, 19.21) * mm});
            skArc(sketch, "E91.1", {"start": v(-29.98, 18.06) * mm, "mid": v(-30.62, 18.62) * mm, "end": v(-31.23, 19.21) * mm});
            skLineSegment(sketch, "E92.0", {"start": v(-13.5, 48.14) * mm, "end": v(-13.5, 36.21) * mm});
            skArc(sketch, "E92.1", {"start": v(-13.5, 36.21) * mm, "mid": v(-14.43, 34.83) * mm, "end": v(-16.06, 35.15) * mm});
            skLineSegment(sketch, "E92.2", {"start": v(-24.5, 43.59) * mm, "end": v(-16.06, 35.15) * mm});
            skArc(sketch, "E93.trimOffspring", {"start": v(-28.83, 40.85) * mm, "mid": v(-35.36, 35.36) * mm, "end": v(-40.85, 28.83) * mm});
            skArc(sketch, "E94", {"start": v(-13.5, 48.14) * mm, "mid": v(-19.13, 46.2) * mm, "end": v(-24.5, 43.59) * mm});
            skArc(sketch, "E95.1.0", {"start": v(-49.27, 8.5) * mm, "mid": v(-50, 0) * mm, "end": v(-49.27, -8.5) * mm});
            skArc(sketch, "E95.1.1", {"start": v(-33.97, 8.43) * mm, "mid": v(-35, 0) * mm, "end": v(-33.97, -8.43) * mm});
            skLineSegment(sketch, "E95.1.2", {"start": v(-49.27, -8.5) * mm, "end": v(-35.67, -8.5) * mm});
            skLineSegment(sketch, "E95.1.3", {"start": v(-49.27, 8.5) * mm, "end": v(-35.67, 8.5) * mm});
            skArc(sketch, "E95.1.4", {"start": v(-35.67, 8.5) * mm, "mid": v(-34.82, 8.48) * mm, "end": v(-33.97, 8.43) * mm});
            skArc(sketch, "E95.1.5", {"start": v(-33.97, -8.43) * mm, "mid": v(-34.82, -8.48) * mm, "end": v(-35.67, -8.5) * mm});
            skLineSegment(sketch, "E95.1.6", {"start": v(-48.14, 13.5) * mm, "end": v(-36.21, 13.5) * mm});
            skArc(sketch, "E95.1.7", {"start": v(-35.15, 16.06) * mm, "mid": v(-34.83, 14.43) * mm, "end": v(-36.21, 13.5) * mm});
            skLineSegment(sketch, "E95.1.8", {"start": v(-43.59, 24.5) * mm, "end": v(-35.15, 16.06) * mm});
            skArc(sketch, "E95.1.9", {"start": v(-43.59, 24.5) * mm, "mid": v(-46.2, 19.13) * mm, "end": v(-48.14, 13.5) * mm});
            skArc(sketch, "E95.2.0", {"start": v(-40.85, -28.83) * mm, "mid": v(-35.36, -35.36) * mm, "end": v(-28.83, -40.85) * mm});
            skArc(sketch, "E95.2.1", {"start": v(-29.98, -18.06) * mm, "mid": v(-24.75, -24.75) * mm, "end": v(-18.06, -29.98) * mm});
            skLineSegment(sketch, "E95.2.2", {"start": v(-28.83, -40.85) * mm, "end": v(-19.21, -31.23) * mm});
            skLineSegment(sketch, "E95.2.3", {"start": v(-40.85, -28.83) * mm, "end": v(-31.23, -19.21) * mm});
            skArc(sketch, "E95.2.4", {"start": v(-31.23, -19.21) * mm, "mid": v(-30.62, -18.62) * mm, "end": v(-29.98, -18.06) * mm});
            skArc(sketch, "E95.2.5", {"start": v(-18.06, -29.98) * mm, "mid": v(-18.62, -30.62) * mm, "end": v(-19.21, -31.23) * mm});
            skLineSegment(sketch, "E95.2.6", {"start": v(-43.59, -24.5) * mm, "end": v(-35.15, -16.06) * mm});
            skArc(sketch, "E95.2.7", {"start": v(-36.21, -13.5) * mm, "mid": v(-34.83, -14.43) * mm, "end": v(-35.15, -16.06) * mm});
            skLineSegment(sketch, "E95.2.8", {"start": v(-48.14, -13.5) * mm, "end": v(-36.21, -13.5) * mm});
            skArc(sketch, "E95.2.9", {"start": v(-48.14, -13.5) * mm, "mid": v(-46.2, -19.13) * mm, "end": v(-43.59, -24.5) * mm});
            skArc(sketch, "E95.3.0", {"start": v(-8.5, -49.27) * mm, "mid": v(0, -50) * mm, "end": v(8.5, -49.27) * mm});
            skArc(sketch, "E95.3.1", {"start": v(-8.43, -33.97) * mm, "mid": v(0, -35) * mm, "end": v(8.43, -33.97) * mm});
            skLineSegment(sketch, "E95.3.2", {"start": v(8.5, -49.27) * mm, "end": v(8.5, -35.67) * mm});
            skLineSegment(sketch, "E95.3.3", {"start": v(-8.5, -49.27) * mm, "end": v(-8.5, -35.67) * mm});
            skArc(sketch, "E95.3.4", {"start": v(-8.5, -35.67) * mm, "mid": v(-8.48, -34.82) * mm, "end": v(-8.43, -33.97) * mm});
            skArc(sketch, "E95.3.5", {"start": v(8.43, -33.97) * mm, "mid": v(8.48, -34.82) * mm, "end": v(8.5, -35.67) * mm});
            skLineSegment(sketch, "E95.3.6", {"start": v(-13.5, -48.14) * mm, "end": v(-13.5, -36.21) * mm});
            skArc(sketch, "E95.3.7", {"start": v(-16.06, -35.15) * mm, "mid": v(-14.43, -34.83) * mm, "end": v(-13.5, -36.21) * mm});
            skLineSegment(sketch, "E95.3.8", {"start": v(-24.5, -43.59) * mm, "end": v(-16.06, -35.15) * mm});
            skArc(sketch, "E95.3.9", {"start": v(-24.5, -43.59) * mm, "mid": v(-19.13, -46.2) * mm, "end": v(-13.5, -48.14) * mm});
            skArc(sketch, "E95.4.0", {"start": v(28.83, -40.85) * mm, "mid": v(35.36, -35.36) * mm, "end": v(40.85, -28.83) * mm});
            skArc(sketch, "E95.4.1", {"start": v(18.06, -29.98) * mm, "mid": v(24.75, -24.75) * mm, "end": v(29.98, -18.06) * mm});
            skLineSegment(sketch, "E95.4.2", {"start": v(40.85, -28.83) * mm, "end": v(31.23, -19.21) * mm});
            skLineSegment(sketch, "E95.4.3", {"start": v(28.83, -40.85) * mm, "end": v(19.21, -31.23) * mm});
            skArc(sketch, "E95.4.4", {"start": v(19.21, -31.23) * mm, "mid": v(18.62, -30.62) * mm, "end": v(18.06, -29.98) * mm});
            skArc(sketch, "E95.4.5", {"start": v(29.98, -18.06) * mm, "mid": v(30.62, -18.62) * mm, "end": v(31.23, -19.21) * mm});
            skLineSegment(sketch, "E95.4.6", {"start": v(24.5, -43.59) * mm, "end": v(16.06, -35.15) * mm});
            skArc(sketch, "E95.4.7", {"start": v(13.5, -36.21) * mm, "mid": v(14.43, -34.83) * mm, "end": v(16.06, -35.15) * mm});
            skLineSegment(sketch, "E95.4.8", {"start": v(13.5, -48.14) * mm, "end": v(13.5, -36.21) * mm});
            skArc(sketch, "E95.4.9", {"start": v(13.5, -48.14) * mm, "mid": v(19.13, -46.2) * mm, "end": v(24.5, -43.59) * mm});
            skArc(sketch, "E95.5.0", {"start": v(49.27, -8.5) * mm, "mid": v(50, 0) * mm, "end": v(49.27, 8.5) * mm});
            skArc(sketch, "E95.5.1", {"start": v(33.97, -8.43) * mm, "mid": v(35, 0) * mm, "end": v(33.97, 8.43) * mm});
            skLineSegment(sketch, "E95.5.2", {"start": v(49.27, 8.5) * mm, "end": v(35.67, 8.5) * mm});
            skLineSegment(sketch, "E95.5.3", {"start": v(49.27, -8.5) * mm, "end": v(35.67, -8.5) * mm});
            skArc(sketch, "E95.5.4", {"start": v(35.67, -8.5) * mm, "mid": v(34.82, -8.48) * mm, "end": v(33.97, -8.43) * mm});
            skArc(sketch, "E95.5.5", {"start": v(33.97, 8.43) * mm, "mid": v(34.82, 8.48) * mm, "end": v(35.67, 8.5) * mm});
            skLineSegment(sketch, "E95.5.6", {"start": v(48.14, -13.5) * mm, "end": v(36.21, -13.5) * mm});
            skArc(sketch, "E95.5.7", {"start": v(35.15, -16.06) * mm, "mid": v(34.83, -14.43) * mm, "end": v(36.21, -13.5) * mm});
            skLineSegment(sketch, "E95.5.8", {"start": v(43.59, -24.5) * mm, "end": v(35.15, -16.06) * mm});
            skArc(sketch, "E95.5.9", {"start": v(43.59, -24.5) * mm, "mid": v(46.2, -19.13) * mm, "end": v(48.14, -13.5) * mm});
            skArc(sketch, "E95.6.0", {"start": v(40.85, 28.83) * mm, "mid": v(35.36, 35.36) * mm, "end": v(28.83, 40.85) * mm});
            skArc(sketch, "E95.6.1", {"start": v(29.98, 18.06) * mm, "mid": v(24.75, 24.75) * mm, "end": v(18.06, 29.98) * mm});
            skLineSegment(sketch, "E95.6.2", {"start": v(28.83, 40.85) * mm, "end": v(19.21, 31.23) * mm});
            skLineSegment(sketch, "E95.6.3", {"start": v(40.85, 28.83) * mm, "end": v(31.23, 19.21) * mm});
            skArc(sketch, "E95.6.4", {"start": v(31.23, 19.21) * mm, "mid": v(30.62, 18.62) * mm, "end": v(29.98, 18.06) * mm});
            skArc(sketch, "E95.6.5", {"start": v(18.06, 29.98) * mm, "mid": v(18.62, 30.62) * mm, "end": v(19.21, 31.23) * mm});
            skLineSegment(sketch, "E95.6.6", {"start": v(43.59, 24.5) * mm, "end": v(35.15, 16.06) * mm});
            skArc(sketch, "E95.6.7", {"start": v(36.21, 13.5) * mm, "mid": v(34.83, 14.43) * mm, "end": v(35.15, 16.06) * mm});
            skLineSegment(sketch, "E95.6.8", {"start": v(48.14, 13.5) * mm, "end": v(36.21, 13.5) * mm});
            skArc(sketch, "E95.6.9", {"start": v(48.14, 13.5) * mm, "mid": v(46.2, 19.13) * mm, "end": v(43.59, 24.5) * mm});
            skArc(sketch, "E95.7.0", {"start": v(8.5, 49.27) * mm, "mid": v(0, 50) * mm, "end": v(-8.5, 49.27) * mm});
            skArc(sketch, "E95.7.1", {"start": v(8.43, 33.97) * mm, "mid": v(0, 35) * mm, "end": v(-8.43, 33.97) * mm});
            skLineSegment(sketch, "E95.7.2", {"start": v(-8.5, 49.27) * mm, "end": v(-8.5, 35.67) * mm});
            skLineSegment(sketch, "E95.7.3", {"start": v(8.5, 49.27) * mm, "end": v(8.5, 35.67) * mm});
            skArc(sketch, "E95.7.4", {"start": v(8.5, 35.67) * mm, "mid": v(8.48, 34.82) * mm, "end": v(8.43, 33.97) * mm});
            skArc(sketch, "E95.7.5", {"start": v(-8.43, 33.97) * mm, "mid": v(-8.48, 34.82) * mm, "end": v(-8.5, 35.67) * mm});
            skLineSegment(sketch, "E95.7.6", {"start": v(13.5, 48.14) * mm, "end": v(13.5, 36.21) * mm});
            skArc(sketch, "E95.7.7", {"start": v(16.06, 35.15) * mm, "mid": v(14.43, 34.83) * mm, "end": v(13.5, 36.21) * mm});
            skLineSegment(sketch, "E95.7.8", {"start": v(24.5, 43.59) * mm, "end": v(16.06, 35.15) * mm});
            skArc(sketch, "E95.7.9", {"start": v(24.5, 43.59) * mm, "mid": v(19.13, 46.2) * mm, "end": v(13.5, 48.14) * mm});
            skSolve(sketch);
        }
        {
            var Q0;
            Q0 = qSketchRegion(id + "F12", true);
            extrude(context, id + "F13", {"entities" : qUnion([Q0]), "operationType" : NewBodyOperationType.ADD, "oppositeDirection" : true, "depth" : 4 * mm});
        }
        {
            var Q0;
            Q0=makeQuery(id+"F1.opRevolve","SWEPT_FACE",FACE,{"disambiguationData":[OSD([sQuery(id+"F0.wireOp",EDGE,"E2")])]});
            var sketch = newSketch(context, id + "F14", { "sketchPlane" : qUnion([Q0])});
            skCircle(sketch, "E96", {"center": v(0, 0) * mm, "radius": 72.4 * mm});
            skCircle(sketch, "E97.0", {"center": v(0, 0) * mm, "radius": 66 * mm});
            skSolve(sketch);
        }
        {
            var Q0;
            Q0 = qSketchRegion(id + "F14", true);
            extrude(context, id + "F15", {"entities" : qUnion([Q0]), "operationType" : NewBodyOperationType.ADD, "oppositeDirection" : true, "depth" : 5.84 * mm});
        }
        {
            var Q0;
            Q0=makeQuery(id+"F15.opExtrude","CAP_EDGE",EDGE,{"disambiguationData":[OSD([sQuery(id+"F14.wireOp",EDGE,"E97.0")])],"isStart":false});
            var Q1;
            Q1=makeQuery(id+"F15.opExtrude","CAP_EDGE",EDGE,{"disambiguationData":[OSD([sQuery(id+"F14.wireOp",EDGE,"E96")])],"isStart":true});
            var Q2;
            Q2=makeQuery(id+"F15.opExtrude","CAP_EDGE",EDGE,{"disambiguationData":[OSD([sQuery(id+"F14.wireOp",EDGE,"E96")])],"isStart":false});
            fillet(context, id + "F16", {"entities" : qUnion([Q0, Q1, Q2]), "radius" : 1 * mm, "tangentPropagation" : true, "allowEdgeOverflow" : false});
        }
    });
